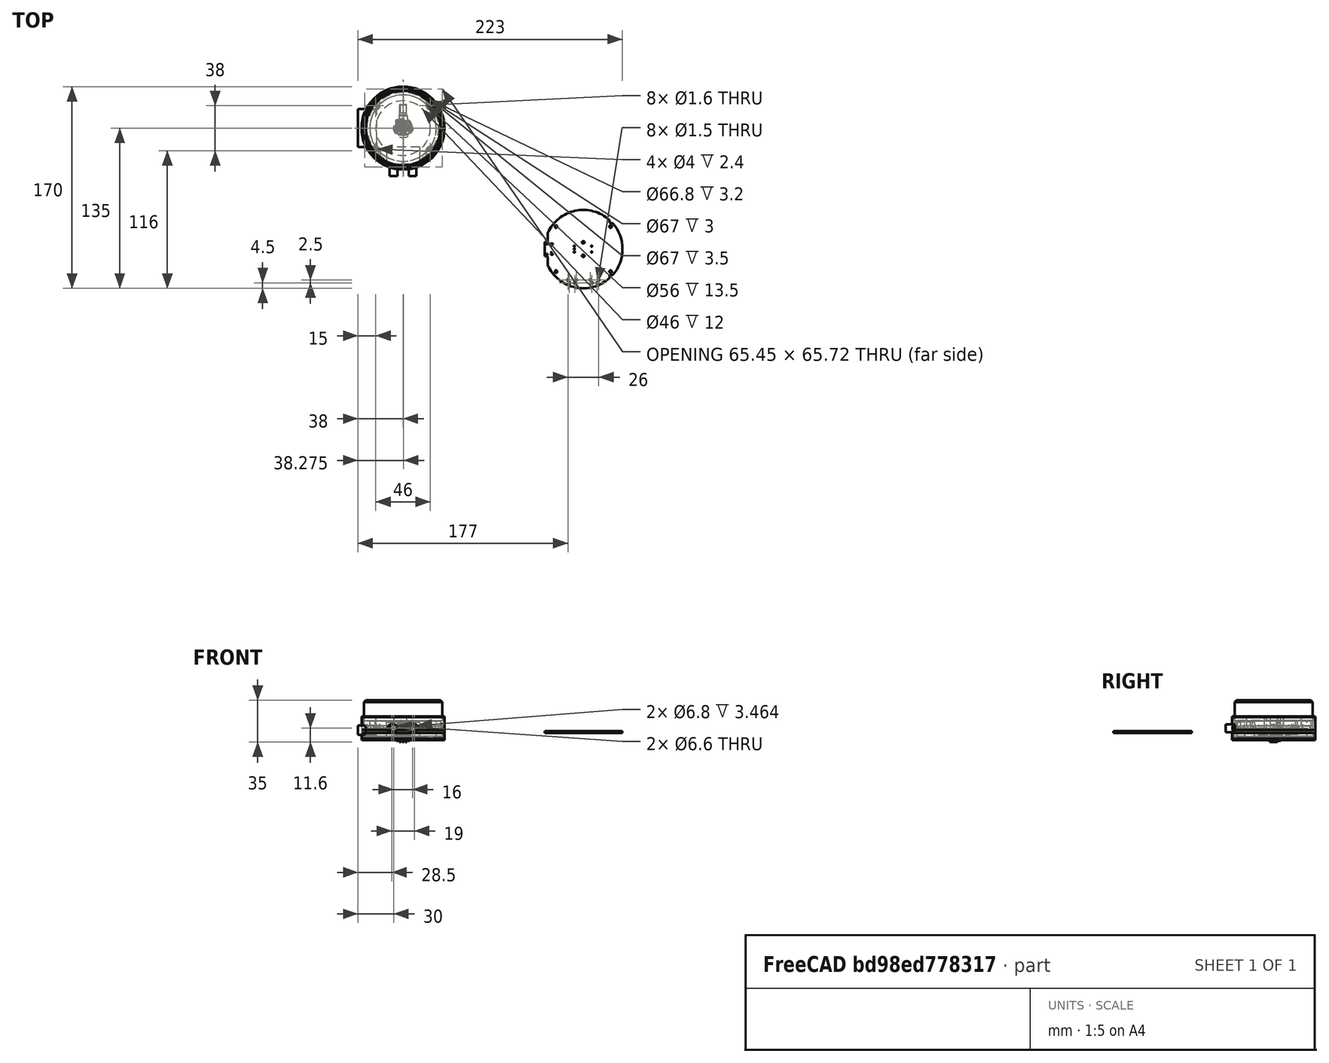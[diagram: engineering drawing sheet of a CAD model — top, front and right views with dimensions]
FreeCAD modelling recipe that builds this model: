
FCSTD DOCUMENT  (FreeCAD 0.18R4 (GitTag))
Label: USBVolumeKnob
License: All rights reserved
LicenseURL: http://en.wikipedia.org/wiki/All_rights_reserved
objects: App::Part×79, Part::Feature×75, Sketcher::SketchObject×22, PartDesign::Pad×10, PartDesign::Pocket×10, PartDesign::Body×6, Mesh::Feature×3, PartDesign::Boolean×2, PartDesign::Revolution×1, PartDesign::Chamfer×1
note: 148 computed .brp shape members not serialized (recipe doc carries the construction recipe); baked Part::Feature solids carry a one-line shape summary decoded from their .brp

FEATURE [Sketcher::SketchObject] Sketch
  MapMode = 5
  Support = -> [XY_Plane028]
  sketch-geometry (1):
    g0: Circle CenterX=0 CenterY=0 CenterZ=0 NormalX=0 NormalY=0 NormalZ=1 AngleXU=0 Radius=33
  constraints (1):
    c: Diameter(g0) = 66
FEATURE [Sketcher::SketchObject] Sketch001
  MapMode = 5
  Support = -> [XY_Plane028]
  sketch-geometry (2):
    g0: ArcOfCircle CenterX=0 CenterY=0 CenterZ=0 NormalX=0 NormalY=0 NormalZ=1 AngleXU=0 Radius=3 StartAngle=4.18879 EndAngle=8.37758
    g1: LineSegment StartX=-1.5 StartY=2.59808 StartZ=0 EndX=-1.5 EndY=-2.59808 EndZ=0
  constraints (7):
    c: Vertical(g1)
    c: Coincident(g0,g1)
    c: Coincident(g0,g1)
    c: Radius(g0) = 3
    c: Coincident(g1,g0)
    c: Coincident(g0,g-1)
    c: DistanceX(g0,g0) = 1.5
FEATURE [PartDesign::Pad] Pad
  Length = 26
  Length2 = 100
  Profile = -> Sketch
  Type = 0
FEATURE [Sketcher::SketchObject] Sketch002
  MapMode = 5
  Placement = pos=(0,0,0) rot=(1,0,0;3.14159rad)
  Support = -> [Pad]
  sketch-geometry (2):
    g0: Circle CenterX=0 CenterY=0 CenterZ=0 NormalX=0 NormalY=0 NormalZ=1 AngleXU=0 Radius=23
    g1: Circle CenterX=0 CenterY=0 CenterZ=0 NormalX=0 NormalY=0 NormalZ=1 AngleXU=0 Radius=8
  constraints (4):
    c: Diameter(g0) = 46
    c: Coincident(g0,g-1)
    c: Diameter(g1) = 16
    c: Coincident(g1,g0)
FEATURE [PartDesign::Pocket] Pocket
  BaseFeature = -> Pad
  Length = 12
  Length2 = 100
  Profile = -> Sketch001
  Reversed = true
  Type = 0
FEATURE [PartDesign::Pocket] Pocket001
  BaseFeature = -> Pocket
  Length = 12
  Length2 = 100
  Profile = -> Sketch002
  Type = 0
FEATURE [Sketcher::SketchObject] Sketch003
  MapMode = 5
  Placement = pos=(0,0,0) rot=(1,0,0;3.14159rad)
  Support = -> [Pocket001]
  sketch-geometry (1):
    g0: Circle CenterX=0 CenterY=0 CenterZ=0 NormalX=0 NormalY=0 NormalZ=1 AngleXU=0 Radius=8
  constraints (2):
    c: Diameter(g0) = 16
    c: Coincident(g0,g-1)
FEATURE [PartDesign::Pocket] Pocket002
  BaseFeature = -> Pocket001
  Length = 2
  Length2 = 100
  Profile = -> Sketch003
  Type = 0
FEATURE [Sketcher::SketchObject] Sketch004
  MapMode = 5
  Support = -> [XY_Plane053]
  sketch-geometry (2):
    g0: ArcOfCircle CenterX=0 CenterY=0 CenterZ=0 NormalX=0 NormalY=0 NormalZ=1 AngleXU=0 Radius=33 StartAngle=3.32443 EndAngle=9.24194
    g1: LineSegment StartX=-32.45 StartY=6 StartZ=0 EndX=-32.45 EndY=-6 EndZ=0
  constraints (7):
    c: Diameter(g0) = 66
    c: Coincident(g0,g-1)
    c: Vertical(g1)
    c: Coincident(g0,g1)
    c: Coincident(g0,g1)
    c: DistanceY(g1,g1) = 12
    c: Coincident(g0,g1)
FEATURE [PartDesign::Pad] Pad001
  Length = 4
  Length2 = 100
  Profile = -> Sketch004
  Type = 0
FEATURE [Sketcher::SketchObject] Sketch006
  MapMode = 5
  Placement = pos=(0,0,0) rot=(1,0,0;1.5708rad)
  Support = -> [XZ_Plane055]
  sketch-geometry (8):
    g0: LineSegment StartX=-35 StartY=-6 StartZ=0 EndX=-33.5 EndY=-6 EndZ=0
    g1: LineSegment StartX=-33.5 StartY=-6 StartZ=0 EndX=-33.5 EndY=-3 EndZ=0
    g2: LineSegment StartX=-33.5 StartY=-3 StartZ=0 EndX=-28 EndY=-3 EndZ=0
    g3: LineSegment StartX=-28 StartY=-3 StartZ=0 EndX=-28 EndY=10.5 EndZ=0
    g4: LineSegment StartX=-28 StartY=10.5 StartZ=0 EndX=-33.5 EndY=10.5 EndZ=0
    g5: LineSegment StartX=-33.5 StartY=10.5 StartZ=0 EndX=-33.5 EndY=14 EndZ=0
    g6: LineSegment StartX=-33.5 StartY=14 StartZ=0 EndX=-35 EndY=14 EndZ=0
    g7: LineSegment StartX=-35 StartY=14 StartZ=0 EndX=-35 EndY=-6 EndZ=0
  constraints (24):
    c: Coincident(g0,g1)
    c: Coincident(g2,g3)
    c: Coincident(g3,g4)
    c: Coincident(g4,g5)
    c: Coincident(g5,g6)
    c: Coincident(g6,g7)
    c: Coincident(g7,g0)
    c: Vertical(g3)
    c: Vertical(g7)
    c: Horizontal(g6)
    c: Horizontal(g4)
    c: Horizontal(g2)
    c: Horizontal(g0)
    c: Vertical(g1)
    c: Vertical(g5)
    c: DistanceX(g0,g-1) = 35
    c: DistanceX(g0,g-1) = 33.5
    c: DistanceX(g2,g-1) = 28
    c: DistanceX(g5,g-1) = 33.5
    c: DistanceY(g0,g-1) = 6
    c: DistanceY(g1,g-1) = 3
    c: DistanceY(g-1,g3) = 10.5
    c: DistanceY(g-1,g6) = 14
    c: Coincident(g2,g1)
FEATURE [PartDesign::Revolution] Revolution
  Angle = 360
  Axis = (0,-2e-16,1)
  Base = (0,0,0)
  Placement = pos=(0,0,0) rot=(1,0,0;1.5708rad)
  Profile = -> Sketch006
  ReferenceAxis = -> Sketch006 [V_Axis]
FEATURE [Sketcher::SketchObject] Sketch007
  MapMode = 5
  Placement = pos=(0,0,0) rot=(1,0,0;1.5708rad)
  Support = -> [XZ_Plane056]
  sketch-geometry (4):
    g0: LineSegment StartX=-14 StartY=-4 StartZ=0 EndX=-14 EndY=9 EndZ=0
    g1: LineSegment StartX=-14 StartY=9 StartZ=0 EndX=14 EndY=9 EndZ=0
    g2: LineSegment StartX=14 StartY=9 StartZ=0 EndX=14 EndY=-4 EndZ=0
    g3: LineSegment StartX=14 StartY=-4 StartZ=0 EndX=-14 EndY=-4 EndZ=0
  constraints (12):
    c: Coincident(g0,g1)
    c: Coincident(g1,g2)
    c: Coincident(g2,g3)
    c: Coincident(g3,g0)
    c: Vertical(g0)
    c: Vertical(g2)
    c: Horizontal(g1)
    c: Horizontal(g3)
    c: DistanceY(g2,g1) = 13
    c: DistanceX(g-1,g1) = 14
    c: DistanceX(g0,g-1) = 14
    c: DistanceY(g2,g-1) = 4
FEATURE [PartDesign::Pad] Pad003
  Length = 14.5
  Length2 = 100
  Placement = pos=(0,0,0) rot=(1,0,0;1.5708rad)
  Profile = -> Sketch007
  Type = 0
FEATURE [Sketcher::SketchObject] Sketch008
  MapMode = 5
  Placement = pos=(0,-14.5,6.4e-15) rot=(1,0,0;1.5708rad)
  Support = -> [Pad003]
  sketch-geometry (2):
    g0: Circle CenterX=-8 CenterY=4 CenterZ=0 NormalX=0 NormalY=0 NormalZ=1 AngleXU=0 Radius=3.3
    g1: Circle CenterX=8 CenterY=4 CenterZ=0 NormalX=0 NormalY=0 NormalZ=1 AngleXU=0 Radius=3.3
  constraints (6):
    c: Radius(g0) = 3.3
    c: Radius(g1) = 3.3
    c: DistanceX(g-1,g1) = 8
    c: DistanceX(g0,g-1) = 8
    c: DistanceY(g-1,g0) = 4
    c: DistanceY(g-1,g1) = 4
FEATURE [PartDesign::Pad] Pad004
  BaseFeature = -> Pad003
  Length = 10
  Length2 = 100
  Placement = pos=(0,0,0) rot=(1,0,0;1.5708rad)
  Profile = -> Sketch008
  Type = 0
FEATURE [PartDesign::Body] Body003
  Group = -> [Sketch007,Pad003,Sketch008,Pad004]
  Origin = -> Origin056
  Placement = pos=(0,-16,0) rot=(0,0,1;0rad)
  Tip = -> Pad004
FEATURE [PartDesign::Boolean] Boolean
  BaseFeature = -> Revolution
  Group = -> [Body003]
  Type = 1
FEATURE [Sketcher::SketchObject] Sketch009
  MapMode = 5
  Placement = pos=(0,0,0) rot=(0.57735,0.57735,0.57735;2.0944rad)
  Support = -> [YZ_Plane057]
  sketch-geometry (4):
    g0: ArcOfCircle CenterX=-12 CenterY=2.4 CenterZ=0 NormalX=0 NormalY=0 NormalZ=1 AngleXU=0 Radius=4 StartAngle=1.5708 EndAngle=4.71239
    g1: ArcOfCircle CenterX=12 CenterY=2.4 CenterZ=0 NormalX=0 NormalY=0 NormalZ=1 AngleXU=0 Radius=4 StartAngle=4.71239 EndAngle=7.85398
    g2: LineSegment StartX=-12 StartY=-1.6 StartZ=0 EndX=12 EndY=-1.6 EndZ=0
    g3: LineSegment StartX=-12 StartY=6.4 StartZ=0 EndX=12 EndY=6.4 EndZ=0
  constraints (10):
    c: Tangent(g0,g3) = 1.5708
    c: Tangent(g0,g2) = -1.5708
    c: Tangent(g2,g1) = -1.5708
    c: Tangent(g3,g1) = 1.5708
    c: Horizontal(g2)
    c: Equal(g0,g1)
    c: Radius(g1) = 4
    c: DistanceX(g0,g1) = 24
    c: DistanceX(g-1,g1) = 12
    c: DistanceY(g1,g-1) = 1.6
FEATURE [PartDesign::Pad] Pad005
  Length = 16
  Length2 = 100
  Placement = pos=(0,0,0) rot=(0.57735,0.57735,0.57735;2.0944rad)
  Profile = -> Sketch009
  Reversed = true
  Type = 0
FEATURE [PartDesign::Body] Body004
  Group = -> [Sketch009,Pad005]
  Origin = -> Origin057
  Placement = pos=(-22,0,0) rot=(0,0,1;0rad)
  Tip = -> Pad005
FEATURE [PartDesign::Boolean] Boolean001
  BaseFeature = -> Boolean
  Group = -> [Body004]
  Type = 1
FEATURE [PartDesign::Body] Body002
  Group = -> [Sketch006,Revolution,Boolean,Boolean001]
  Origin = -> Origin055
  Tip = -> Boolean001
FEATURE [App::Part] Part003  label="OldMidFrame"
  Group = -> [Body002]
  Origin = -> Origin054
FEATURE [Part::Feature] Part__Feature017  label="SOLID014"
  shape: bbox 1.6 x 0.8 x 0.45 mm, 26 faces (baked)
FEATURE [Part::Feature] Part__Feature029  label="SOLID026"
  shape: bbox 1.6 x 0.8 x 0.45 mm, 26 faces (baked)
FEATURE [Part::Feature] Part__Feature037  label="SOLID034"
  shape: bbox 1.6 x 0.8 x 0.8 mm, 28 faces (baked)
FEATURE [Part::Feature] Part__Feature005  label="SOLID003"
  shape: bbox 10.15 x 5.2 x 3.4 mm, 195 faces (baked)
FEATURE [Part::Feature] Part__Feature054  label="SOLID051"
  shape: bbox 1.6 x 0.8 x 0.8 mm, 28 faces (baked)
FEATURE [Part::Feature] Part__Feature032  label="SOLID029"
  shape: bbox 1.6 x 0.8 x 0.45 mm, 26 faces (baked)
FEATURE [Part::Feature] Part__Feature058  label="SOLID055"
  shape: bbox 1.6 x 0.8 x 0.8 mm, 28 faces (baked)
FEATURE [Part::Feature] Part__Feature057  label="SOLID054"
  shape: bbox 2 x 1.25 x 1.25 mm, 28 faces (baked)
FEATURE [Part::Feature] Part__Feature025  label="SOLID022"
  shape: bbox 1.6 x 0.8 x 0.45 mm, 26 faces (baked)
FEATURE [Part::Feature] Part__Feature004  label="SOLID002"
  shape: bbox 16.4 x 5.2 x 3.4 mm, 320 faces (baked)
FEATURE [Part::Feature] Part__Feature049  label="SOLID046"
  shape: bbox 1 x 0.5 x 0.5 mm, 28 faces (baked)
FEATURE [Part::Feature] Part__Feature011  label="SOLID009"
  shape: bbox 7 x 6.5 x 1.7 mm, 78 faces (baked)
FEATURE [Part::Feature] Part__Feature013  label="SOLID011"
  shape: bbox 4 x 2.5 x 1.59 mm, 242 faces (baked)
FEATURE [Part::Feature] Part__Feature014  label="COMPOUND002"
  shape: bbox 8.7 x 10.9 x 12.85 mm, 158 faces, 3 solids (baked)
FEATURE [Part::Feature] Part__Feature002  label="SOLID"
  shape: bbox 14 x 23.5 x 14.75 mm, 198 faces (baked)
FEATURE [Part::Feature] Part__Feature016  label="SOLID013"
  shape: bbox 1.6 x 0.8 x 0.45 mm, 26 faces (baked)
FEATURE [Part::Feature] Part__Feature008  label="SOLID006"
  shape: bbox 12 x 12 x 1.5 mm, 1004 faces (baked)
FEATURE [Part::Feature] Part__Feature001  label="COMPOUND001"
  shape: bbox 6.35 x 6.121 x 5.842 mm, 252 faces, 3 solids (baked)
FEATURE [Part::Feature] Part__Feature006  label="SOLID004"
  shape: bbox 5 x 1.113 x 3.175 mm, 141 faces (baked)
FEATURE [Part::Feature] Part__Feature010  label="SOLID008"
  shape: bbox 2.8 x 2.9 x 1.55 mm, 109 faces (baked)
FEATURE [App::Part] Molex_PicoBlade_53261_0471_1x04_1MP_P1_25mm_Horizontal  label="Molex_PicoBlade_53261-0471_1x04-1MP_P1.25mm_Horizontal"
  Group = -> [Part__Feature005]
  Origin = -> Origin006
  Placement = pos=(176.75,-93,1.65) rot=(0,0,1;1.5708rad)
FEATURE [App::Part] SOT_23_5001  label="SOT-23-007"
  Group = -> [Part__Feature010]
  Origin = -> Origin011
  Placement = pos=(169,-80.25,1.65) rot=(0,0,1;0rad)
FEATURE [App::Part] SW_SPST_B3U_1000P001  label="SW_SPST_B3U-1000P001"
  Group = -> [Part__Feature013]
  Origin = -> Origin014
  Placement = pos=(164,-96,1.65) rot=(0,0,-1;1.5708rad)
FEATURE [App::Part] SOT_223  label="SOT-223"
  Group = -> [Part__Feature011]
  Origin = -> Origin012
  Placement = pos=(136.5,-110,1.65) rot=(0,0,1;0rad)
FEATURE [App::Part] FTSH_105_01_L_DV_K  label="FTSH-105-01-L-DV-K"
  Group = -> [Part__Feature001]
  Origin = -> Origin002
  Placement = pos=(135.75,-83,2.05) rot=(-0.57735,0.57735,0.57735;4.18879rad)
FEATURE [App::Part] pec12r_4020f_n0024  label="pec12r-4020f-n0024"
  Group = -> [Part__Feature002]
  Origin = -> Origin003
  Placement = pos=(152,-102,1.65) rot=(0.57735,0.57735,0.57735;2.0944rad)
FEATURE [App::Part] Molex_PicoBlade_53261_0971_1x09_1MP_P1_25mm_Horizontal  label="Molex_PicoBlade_53261-0971_1x09-1MP_P1.25mm_Horizontal"
  Group = -> [Part__Feature004]
  Origin = -> Origin005
  Placement = pos=(176.75,-108.25,1.65) rot=(0,0,1;1.5708rad)
FEATURE [App::Part] ABM3B_18_432MHZ_B2  label="ABM3B-18.432MHZ-B2"
  Group = -> [Part__Feature006]
  Origin = -> Origin007
  Placement = pos=(163.25,-87,1.65) rot=(-0.57735,0.57735,0.57735;4.18879rad)
FEATURE [App::Part] LQFP_64_10x10mm_P0_5mm  label="LQFP-64_10x10mm_P0.5mm"
  Group = -> [Part__Feature008]
  Origin = -> Origin009
  Placement = pos=(149.5,-84.5,1.65) rot=(0,0,1;3.14159rad)
FEATURE [App::Part] B3F_3152__3DModel_STEP_273799  label="B3F-3152--3DModel-STEP-273799"
  Group = -> [Part__Feature014]
  Origin = -> Origin015
  Placement = pos=(163.75,-130.5,1.65) rot=(1,0,0;1.5708rad)
FEATURE [App::Part] R_0603_1608Metric001
  Group = -> [Part__Feature016]
  Origin = -> Origin017
  Placement = pos=(171.5,-111.75,1.65) rot=(0,0,1;1.5708rad)
FEATURE [App::Part] R_0603_1608Metric002
  Group = -> [Part__Feature017]
  Origin = -> Origin018
  Placement = pos=(130.5,-104.75,1.65) rot=(0,0,1;0rad)
FEATURE [App::Part] R_0603_1608Metric010
  Group = -> [Part__Feature025]
  Origin = -> Origin026
  Placement = pos=(162,-91.75,1.65) rot=(0,0,1;1.5708rad)
FEATURE [App::Part] R_0603_1608Metric017
  Group = -> [Part__Feature032]
  Origin = -> Origin033
  Placement = pos=(161.5,-122.75,1.65) rot=(0,0,1;1.5708rad)
FEATURE [App::Part] C_0603_1608Metric
  Group = -> [Part__Feature037]
  Origin = -> Origin038
  Placement = pos=(168.5,-92.5,-0.05) rot=(0.866025,-0.5,0;3.14159rad)
FEATURE [App::Part] R_0603_1608Metric014
  Group = -> [Part__Feature029]
  Origin = -> Origin030
  Placement = pos=(139,-93,1.65) rot=(0,0,1;3.14159rad)
FEATURE [App::Part] C_0603_1608Metric016
  Group = -> [Part__Feature058]
  Origin = -> Origin059
  Placement = pos=(169,-91,1.65) rot=(0,0,1;1.5708rad)
FEATURE [App::Part] C_0603_1608Metric015
  Group = -> [Part__Feature054]
  Origin = -> Origin079
  Placement = pos=(166.5,-84.5,1.65) rot=(0,0,1;1.5708rad)
FEATURE [App::Part] C_0805_2012Metric002
  Group = -> [Part__Feature057]
  Origin = -> Origin058
  Placement = pos=(130.75,-112,1.65) rot=(0,0,1;1.5708rad)
FEATURE [App::Part] C_0402_1005Metric001
  Group = -> [Part__Feature049]
  Origin = -> Origin050
  Placement = pos=(160.25,-88.25,1.65) rot=(0,0,1;1.5708rad)
FEATURE [Part::Feature] Part__Feature  label="COMPOUND"
  shape: bbox 8.941 x 4.361 x 6.901 mm, 1244 faces, 44 solids (baked)
FEATURE [App::Part] DX07S016JA1R1500__3DModel_STEP_1  label="DX07S016JA1R1500--3DModel-STEP-1"
  Group = -> [Part__Feature]
  Origin = -> Origin001
  Placement = pos=(122.75,-102,1.75) rot=(-0.57735,0.57735,0.57735;4.18879rad)
FEATURE [Part::Feature] Part__Feature003  label="SOLID001"
  shape: bbox 5.4 x 5 x 1.5 mm, 60 faces (baked)
FEATURE [App::Part] LED_RGB_5050_6  label="LED_RGB_5050-6"
  Group = -> [Part__Feature003]
  Origin = -> Origin004
  Placement = pos=(132,-113.5,-0.05) rot=(0.866025,-0.5,0;3.14159rad)
FEATURE [Part::Feature] Part__Feature012  label="SOLID010"
  shape: bbox 4 x 2.5 x 1.59 mm, 242 faces (baked)
FEATURE [App::Part] SW_SPST_B3U_1000P  label="SW_SPST_B3U-1000P"
  Group = -> [Part__Feature012]
  Origin = -> Origin013
  Placement = pos=(168.75,-96,1.65) rot=(0,0,-1;1.5708rad)
FEATURE [Part::Feature] Part__Feature074  label="COMPOUND004"
  shape: bbox 65.6 x 66 x 1.6 mm, 61 faces (baked)
FEATURE [Part::Feature] Part__Feature070  label="SOLID066"
  shape: bbox 5.4 x 5 x 1.5 mm, 60 faces (baked)
FEATURE [App::Part] LED_RGB_5050_6005  label="LED_RGB_5050-011"
  Group = -> [Part__Feature070]
  Origin = -> Origin071
  Placement = pos=(152,-125,-0.05) rot=(1,0,0;3.14159rad)
FEATURE [Part::Feature] Part__Feature069  label="SOLID065"
  shape: bbox 1.6 x 0.8 x 0.45 mm, 26 faces (baked)
FEATURE [App::Part] R_0603_1608Metric024
  Group = -> [Part__Feature069]
  Origin = -> Origin070
  Placement = pos=(142.5,-122.75,1.65) rot=(0,0,1;1.5708rad)
FEATURE [Part::Feature] Part__Feature071  label="SOLID067"
  shape: bbox 1.6 x 0.8 x 0.8 mm, 28 faces (baked)
FEATURE [App::Part] C_0603_1608Metric019
  Group = -> [Part__Feature071]
  Origin = -> Origin072
  Placement = pos=(163,-122.75,1.65) rot=(0,0,-1;1.5708rad)
FEATURE [Part::Feature] Part__Feature060  label="SOLID057"
  shape: bbox 1.6 x 0.8 x 0.8 mm, 28 faces (baked)
FEATURE [App::Part] C_0603_1608Metric017
  Group = -> [Part__Feature060]
  Origin = -> Origin061
  Placement = pos=(139,-94.5,1.65) rot=(0,0,1;3.14159rad)
FEATURE [Part::Feature] Part__Feature064  label="SOLID060"
  shape: bbox 1.6 x 0.8 x 0.45 mm, 26 faces (baked)
FEATURE [App::Part] R_0603_1608Metric019
  Group = -> [Part__Feature064]
  Origin = -> Origin065
  Placement = pos=(139,-100.5,1.65) rot=(0,0,1;3.14159rad)
FEATURE [Part::Feature] Part__Feature053  label="SOLID050"
  shape: bbox 1.6 x 0.8 x 0.8 mm, 28 faces (baked)
FEATURE [App::Part] C_0603_1608Metric014
  Group = -> [Part__Feature053]
  Origin = -> Origin076
  Placement = pos=(158.75,-81.5,1.65) rot=(0,0,1;0rad)
FEATURE [Part::Feature] Part__Feature059  label="SOLID056"
  shape: bbox 2 x 1.25 x 1.25 mm, 28 faces (baked)
FEATURE [App::Part] C_0805_2012Metric003
  Group = -> [Part__Feature059]
  Origin = -> Origin060
  Placement = pos=(130.75,-108,1.65) rot=(0,0,-1;1.5708rad)
FEATURE [Part::Feature] Part__Feature065  label="SOLID061"
  shape: bbox 1.6 x 0.8 x 0.45 mm, 26 faces (baked)
FEATURE [App::Part] R_0603_1608Metric020
  Group = -> [Part__Feature065]
  Origin = -> Origin066
  Placement = pos=(139,-99,1.65) rot=(0,0,1;3.14159rad)
FEATURE [Part::Feature] Part__Feature067  label="SOLID063"
  shape: bbox 1.6 x 0.8 x 0.45 mm, 26 faces (baked)
FEATURE [App::Part] R_0603_1608Metric022
  Group = -> [Part__Feature067]
  Origin = -> Origin068
  Placement = pos=(139,-97.5,1.65) rot=(0,0,1;0rad)
FEATURE [Part::Feature] Part__Feature061  label="SOLID058"
  shape: bbox 1.6 x 0.8 x 0.8 mm, 28 faces (baked)
FEATURE [App::Part] C_0603_1608Metric018
  Group = -> [Part__Feature061]
  Origin = -> Origin062
  Placement = pos=(139,-96,1.65) rot=(0,0,1;3.14159rad)
FEATURE [Part::Feature] Part__Feature063  label="COMPOUND003"
  shape: bbox 8.7 x 10.9 x 12.85 mm, 158 faces, 3 solids (baked)
FEATURE [App::Part] B3F_3152__3DModel_STEP_273799001  label="B3F-3152--3DModel-STEP-273800"
  Group = -> [Part__Feature063]
  Origin = -> Origin064
  Placement = pos=(144.75,-130.5,1.65) rot=(1,0,0;1.5708rad)
FEATURE [Part::Feature] Part__Feature068  label="SOLID064"
  shape: bbox 1.6 x 0.8 x 0.45 mm, 26 faces (baked)
FEATURE [App::Part] R_0603_1608Metric023
  Group = -> [Part__Feature068]
  Origin = -> Origin069
  Placement = pos=(141,-122.75,1.65) rot=(0,0,-1;1.5708rad)
FEATURE [Part::Feature] Part__Feature066  label="SOLID062"
  shape: bbox 1.6 x 0.8 x 0.45 mm, 26 faces (baked)
FEATURE [App::Part] R_0603_1608Metric021
  Group = -> [Part__Feature066]
  Origin = -> Origin067
  Placement = pos=(139,-102,1.65) rot=(0,0,1;0rad)
FEATURE [Part::Feature] Part__Feature055  label="SOLID052"
  shape: bbox 2 x 1.25 x 1.25 mm, 28 faces (baked)
FEATURE [App::Part] C_0805_2012Metric
  Group = -> [Part__Feature055]
  Origin = -> Origin080
  Placement = pos=(148.5,-75,1.65) rot=(0,0,1;1.5708rad)
FEATURE [Part::Feature] Part__Feature052  label="SOLID049"
  shape: bbox 1.6 x 0.8 x 0.8 mm, 28 faces (baked)
FEATURE [App::Part] C_0603_1608Metric013
  Group = -> [Part__Feature052]
  Origin = -> Origin077
  Placement = pos=(158.75,-80,1.65) rot=(0,0,1;0rad)
FEATURE [Part::Feature] Part__Feature062  label="SOLID059"
  shape: bbox 1.6 x 0.8 x 0.45 mm, 26 faces (baked)
FEATURE [App::Part] R_0603_1608Metric018
  Group = -> [Part__Feature062]
  Origin = -> Origin063
  Placement = pos=(130.5,-99.25,1.65) rot=(0,0,1;0rad)
FEATURE [Part::Feature] Part__Feature042  label="SOLID039"
  shape: bbox 1.6 x 0.8 x 0.8 mm, 28 faces (baked)
FEATURE [App::Part] C_0603_1608Metric005
  Group = -> [Part__Feature042]
  Origin = -> Origin043
  Placement = pos=(152,-83,-0.05) rot=(1,0,0;3.14159rad)
FEATURE [Part::Feature] Part__Feature046  label="SOLID043"
  shape: bbox 1.6 x 0.8 x 0.8 mm, 28 faces (baked)
FEATURE [App::Part] C_0603_1608Metric009
  Group = -> [Part__Feature046]
  Origin = -> Origin047
  Placement = pos=(144,-75.25,1.65) rot=(0,0,1;1.5708rad)
FEATURE [Part::Feature] Part__Feature051  label="SOLID048"
  shape: bbox 1.6 x 0.8 x 0.8 mm, 28 faces (baked)
FEATURE [App::Part] C_0603_1608Metric012
  Group = -> [Part__Feature051]
  Origin = -> Origin052
  Placement = pos=(157.75,-90.5,1.65) rot=(0,0,-1;1.5708rad)
FEATURE [Part::Feature] Part__Feature040  label="SOLID037"
  shape: bbox 1.6 x 0.8 x 0.8 mm, 28 faces (baked)
FEATURE [App::Part] C_0603_1608Metric003
  Group = -> [Part__Feature040]
  Origin = -> Origin041
  Placement = pos=(135.5,-111.5,-0.05) rot=(0.5,0.866025,0;3.14159rad)
FEATURE [Part::Feature] Part__Feature041  label="SOLID038"
  shape: bbox 1.6 x 0.8 x 0.8 mm, 28 faces (baked)
FEATURE [App::Part] C_0603_1608Metric004
  Group = -> [Part__Feature041]
  Origin = -> Origin042
  Placement = pos=(135.5,-92.5,-0.05) rot=(0.866025,0.5,0;3.14159rad)
FEATURE [Part::Feature] Part__Feature036  label="SOLID033"
  shape: bbox 5.4 x 5 x 1.5 mm, 60 faces (baked)
FEATURE [App::Part] LED_RGB_5050_6004  label="LED_RGB_5050-010"
  Group = -> [Part__Feature036]
  Origin = -> Origin037
  Placement = pos=(152,-79,-0.05) rot=(0,1,0;3.14159rad)
FEATURE [Part::Feature] Part__Feature043  label="SOLID040"
  shape: bbox 1.6 x 0.8 x 0.8 mm, 28 faces (baked)
FEATURE [App::Part] C_0603_1608Metric006
  Group = -> [Part__Feature043]
  Origin = -> Origin044
  Placement = pos=(168.25,-77.5,1.65) rot=(0,0,1;3.14159rad)
FEATURE [Part::Feature] Part__Feature047  label="SOLID044"
  shape: bbox 1.6 x 0.8 x 0.8 mm, 28 faces (baked)
FEATURE [App::Part] C_0603_1608Metric010
  Group = -> [Part__Feature047]
  Origin = -> Origin048
  Placement = pos=(141.25,-89,1.65) rot=(0,0,1;1.5708rad)
FEATURE [Part::Feature] Part__Feature038  label="SOLID035"
  shape: bbox 1.6 x 0.8 x 0.8 mm, 28 faces (baked)
FEATURE [App::Part] C_0603_1608Metric001
  Group = -> [Part__Feature038]
  Origin = -> Origin039
  Placement = pos=(168.5,-111.5,-0.05) rot=(-0.5,0.866025,0;3.14159rad)
FEATURE [Part::Feature] Part__Feature039  label="SOLID036"
  shape: bbox 1.6 x 0.8 x 0.8 mm, 28 faces (baked)
FEATURE [App::Part] C_0603_1608Metric002
  Group = -> [Part__Feature039]
  Origin = -> Origin040
  Placement = pos=(152,-121,-0.05) rot=(0,1,0;3.14159rad)
FEATURE [Part::Feature] Part__Feature045  label="SOLID042"
  shape: bbox 1.6 x 0.8 x 0.8 mm, 28 faces (baked)
FEATURE [App::Part] C_0603_1608Metric008
  Group = -> [Part__Feature045]
  Origin = -> Origin046
  Placement = pos=(153.5,-76.25,1.65) rot=(0,0,1;0rad)
FEATURE [Part::Feature] Part__Feature048  label="SOLID045"
  shape: bbox 1 x 0.5 x 0.5 mm, 28 faces (baked)
FEATURE [App::Part] C_0402_1005Metric
  Group = -> [Part__Feature048]
  Origin = -> Origin049
  Placement = pos=(160.25,-86,1.65) rot=(0,0,1;1.5708rad)
FEATURE [Part::Feature] Part__Feature050  label="SOLID047"
  shape: bbox 1.6 x 0.8 x 0.8 mm, 28 faces (baked)
FEATURE [App::Part] C_0603_1608Metric011
  Group = -> [Part__Feature050]
  Origin = -> Origin051
  Placement = pos=(155.25,-92.75,1.65) rot=(0,0,1;3.14159rad)
FEATURE [Part::Feature] Part__Feature073  label="SOLID069"
  shape: bbox 1.6 x 0.8 x 0.8 mm, 28 faces (baked)
FEATURE [App::Part] C_0603_1608Metric021
  Group = -> [Part__Feature073]
  Origin = -> Origin074
  Placement = pos=(144,-122.75,1.65) rot=(0,0,-1;1.5708rad)
FEATURE [Part::Feature] Part__Feature022  label="SOLID019"
  shape: bbox 1.6 x 0.8 x 0.45 mm, 26 faces (baked)
FEATURE [App::Part] R_0603_1608Metric007
  Group = -> [Part__Feature022]
  Origin = -> Origin023
  Placement = pos=(163.25,-83.25,1.65) rot=(0,0,1;0rad)
FEATURE [Part::Feature] Part__Feature072  label="SOLID068"
  shape: bbox 1.6 x 0.8 x 0.8 mm, 28 faces (baked)
FEATURE [App::Part] C_0603_1608Metric020
  Group = -> [Part__Feature072]
  Origin = -> Origin073
  Placement = pos=(139,-103.5,1.65) rot=(0,0,1;3.14159rad)
FEATURE [Part::Feature] Part__Feature033  label="SOLID030"
  shape: bbox 5.4 x 5 x 1.5 mm, 60 faces (baked)
FEATURE [App::Part] LED_RGB_5050_6001  label="LED_RGB_5050-007"
  Group = -> [Part__Feature033]
  Origin = -> Origin034
  Placement = pos=(172,-90.5,-0.05) rot=(0.5,0.866025,0;3.14159rad)
FEATURE [Part::Feature] Part__Feature019  label="SOLID016"
  shape: bbox 1.6 x 0.8 x 0.45 mm, 26 faces (baked)
FEATURE [App::Part] R_0603_1608Metric004
  Group = -> [Part__Feature019]
  Origin = -> Origin020
  Placement = pos=(130.5,-95.75,1.65) rot=(0,0,1;3.14159rad)
FEATURE [Part::Feature] Part__Feature023  label="SOLID020"
  shape: bbox 1.6 x 0.8 x 0.45 mm, 26 faces (baked)
FEATURE [App::Part] R_0603_1608Metric008
  Group = -> [Part__Feature023]
  Origin = -> Origin024
  Placement = pos=(168.25,-84.5,1.65) rot=(0,0,1;1.5708rad)
FEATURE [Part::Feature] Part__Feature024  label="SOLID021"
  shape: bbox 1.6 x 0.8 x 0.45 mm, 26 faces (baked)
FEATURE [App::Part] R_0603_1608Metric009
  Group = -> [Part__Feature024]
  Origin = -> Origin083
  Placement = pos=(166.5,-88,1.65) rot=(0,0,1;1.5708rad)
FEATURE [Part::Feature] Part__Feature018  label="SOLID015"
  shape: bbox 1.6 x 0.8 x 0.45 mm, 26 faces (baked)
FEATURE [App::Part] R_0603_1608Metric003
  Group = -> [Part__Feature018]
  Origin = -> Origin019
  Placement = pos=(130.5,-97.5,1.65) rot=(0,0,1;0rad)
FEATURE [Part::Feature] Part__Feature021  label="SOLID018"
  shape: bbox 1.6 x 0.8 x 0.45 mm, 26 faces (baked)
FEATURE [App::Part] R_0603_1608Metric006
  Group = -> [Part__Feature021]
  Origin = -> Origin022
  Placement = pos=(152.75,-74.5,1.65) rot=(0,0,1;3.14159rad)
FEATURE [Part::Feature] Part__Feature027  label="SOLID024"
  shape: bbox 1.6 x 0.8 x 0.45 mm, 26 faces (baked)
FEATURE [App::Part] R_0603_1608Metric012
  Group = -> [Part__Feature027]
  Origin = -> Origin081
  Placement = pos=(134.75,-114.5,1.65) rot=(0,0,1;3.14159rad)
FEATURE [Part::Feature] Part__Feature031  label="SOLID028"
  shape: bbox 1.6 x 0.8 x 0.45 mm, 26 faces (baked)
FEATURE [App::Part] R_0603_1608Metric016
  Group = -> [Part__Feature031]
  Origin = -> Origin032
  Placement = pos=(160,-122.75,1.65) rot=(0,0,-1;1.5708rad)
FEATURE [Part::Feature] Part__Feature020  label="SOLID017"
  shape: bbox 1.6 x 0.8 x 0.45 mm, 26 faces (baked)
FEATURE [App::Part] R_0603_1608Metric005
  Group = -> [Part__Feature020]
  Origin = -> Origin021
  Placement = pos=(152.75,-73,1.65) rot=(0,0,1;0rad)
FEATURE [Part::Feature] Part__Feature026  label="SOLID023"
  shape: bbox 1.6 x 0.8 x 0.45 mm, 26 faces (baked)
FEATURE [App::Part] R_0603_1608Metric011
  Group = -> [Part__Feature026]
  Origin = -> Origin082
  Placement = pos=(170.5,-91,1.65) rot=(0,0,-1;1.5708rad)
FEATURE [Part::Feature] Part__Feature028  label="SOLID025"
  shape: bbox 1.6 x 0.8 x 0.45 mm, 26 faces (baked)
FEATURE [App::Part] R_0603_1608Metric013
  Group = -> [Part__Feature028]
  Origin = -> Origin029
  Placement = pos=(134.75,-105.5,1.65) rot=(0,0,1;3.14159rad)
FEATURE [Part::Feature] Part__Feature034  label="SOLID031"
  shape: bbox 5.4 x 5 x 1.5 mm, 60 faces (baked)
FEATURE [App::Part] LED_RGB_5050_6002  label="LED_RGB_5050-008"
  Group = -> [Part__Feature034]
  Origin = -> Origin035
  Placement = pos=(172,-113.5,-0.05) rot=(0.866025,0.5,0;3.14159rad)
FEATURE [Part::Feature] Part__Feature035  label="SOLID032"
  shape: bbox 5.4 x 5 x 1.5 mm, 60 faces (baked)
FEATURE [App::Part] LED_RGB_5050_6003  label="LED_RGB_5050-009"
  Group = -> [Part__Feature035]
  Origin = -> Origin036
  Placement = pos=(132,-90.5,-0.05) rot=(-0.5,0.866025,0;3.14159rad)
FEATURE [Part::Feature] Part__Feature044  label="SOLID041"
  shape: bbox 1.6 x 0.8 x 0.8 mm, 28 faces (baked)
FEATURE [App::Part] C_0603_1608Metric007
  Group = -> [Part__Feature044]
  Origin = -> Origin045
  Placement = pos=(162.75,-77.5,1.65) rot=(0,0,1;3.14159rad)
FEATURE [Part::Feature] Part__Feature007  label="SOLID005"
  shape: bbox 2.8 x 2.9 x 1.55 mm, 124 faces (baked)
FEATURE [App::Part] SOT_23_6  label="SOT-23-6"
  Group = -> [Part__Feature007]
  Origin = -> Origin008
  Placement = pos=(130.75,-102,1.65) rot=(0,0,1;0rad)
FEATURE [Part::Feature] Part__Feature009  label="SOLID007"
  shape: bbox 2.8 x 2.9 x 1.55 mm, 109 faces (baked)
FEATURE [App::Part] SOT_23_5  label="SOT-23-5"
  Group = -> [Part__Feature009]
  Origin = -> Origin010
  Placement = pos=(163.5,-80.25,1.65) rot=(0,0,1;0rad)
FEATURE [Part::Feature] Part__Feature015  label="SOLID012"
  shape: bbox 1.6 x 0.8 x 0.45 mm, 26 faces (baked)
FEATURE [App::Part] R_0603_1608Metric
  Group = -> [Part__Feature015]
  Origin = -> Origin016
  Placement = pos=(170,-111.75,1.65) rot=(0,0,1;1.5708rad)
FEATURE [Part::Feature] Part__Feature030  label="SOLID027"
  shape: bbox 1.6 x 0.8 x 0.45 mm, 26 faces (baked)
FEATURE [App::Part] R_0603_1608Metric015
  Group = -> [Part__Feature030]
  Origin = -> Origin031
  Placement = pos=(139,-91.5,1.65) rot=(0,0,1;3.14159rad)
FEATURE [Part::Feature] Part__Feature056  label="SOLID053"
  shape: bbox 2 x 1.25 x 1.25 mm, 28 faces (baked)
FEATURE [App::Part] C_0805_2012Metric001
  Group = -> [Part__Feature056]
  Origin = -> Origin078
  Placement = pos=(146.5,-75,1.65) rot=(0,0,1;1.5708rad)
FEATURE [App::Part] Open_CASCADE_STEP_translator_6_9_1  label="PCBA"
  Group = -> [DX07S016JA1R1500__3DModel_STEP_1,FTSH_105_01_L_DV_K,pec12r_4020f_n0024,LED_RGB_5050_6,Molex_PicoBlade_53261_0971_1x09_1MP_P1_25mm_Horizontal,Molex_PicoBlade_53261_0471_1x04_1MP_P1_25mm_Horizontal,ABM3B_18_432MHZ_B2,SOT_23_6,LQFP_64_10x10mm_P0_5mm,SOT_23_5,SOT_23_5001,SOT_223,SW_SPST_B3U_1000P,SW_SPST_B3U_1000P001,B3F_3152__3DModel_STEP_273799,R_0603_1608Metric,R_0603_1608Metric001,+58 more]
  Origin = -> Origin075
  Placement = pos=(-152,102,-1.6) rot=(0,0,1;0rad)
FEATURE [Sketcher::SketchObject] Sketch011  label="BoardOutline"
  MapMode = 5
  sketch-geometry (16):
    g0: ArcOfCircle CenterX=0 CenterY=0 CenterZ=0 NormalX=0 NormalY=0 NormalZ=1 AngleXU=0 Radius=33 StartAngle=3.57129 EndAngle=5.44212
    g1: LineSegment StartX=-32.6 StartY=6 StartZ=0 EndX=-32.6 EndY=-6 EndZ=0
    g2: LineSegment StartX=22 StartY=-24.5967 StartZ=0 EndX=22 EndY=-23 EndZ=0
    g3: LineSegment StartX=23 StartY=-22 StartZ=0 EndX=24.5967 EndY=-22 EndZ=0
    g4: ArcOfCircle CenterX=23 CenterY=-23 CenterZ=0 NormalX=0 NormalY=0 NormalZ=1 AngleXU=0 Radius=1 StartAngle=1.5708 EndAngle=3.14159
    g5: LineSegment StartX=22 StartY=24.5967 StartZ=0 EndX=22 EndY=23 EndZ=0
    g6: LineSegment StartX=23 StartY=22 StartZ=0 EndX=24.5967 EndY=22 EndZ=0
    g7: ArcOfCircle CenterX=23 CenterY=23 CenterZ=0 NormalX=0 NormalY=0 NormalZ=1 AngleXU=0 Radius=1 StartAngle=3.14159 EndAngle=4.71239
    g8: LineSegment StartX=-32.6 StartY=6 StartZ=0 EndX=-31 EndY=6 EndZ=0
    g9: LineSegment StartX=-30 StartY=7 StartZ=0 EndX=-30 EndY=13.7477 EndZ=0
    g10: ArcOfCircle CenterX=-31 CenterY=7 CenterZ=0 NormalX=0 NormalY=0 NormalZ=1 AngleXU=0 Radius=1 StartAngle=4.71239 EndAngle=6.28319
    g11: LineSegment StartX=-32.6 StartY=-6 StartZ=0 EndX=-31 EndY=-6 EndZ=0
    g12: LineSegment StartX=-30 StartY=-7 StartZ=0 EndX=-30 EndY=-13.7477 EndZ=0
    g13: ArcOfCircle CenterX=-31 CenterY=-7 CenterZ=0 NormalX=0 NormalY=0 NormalZ=1 AngleXU=0 Radius=1 StartAngle=0 EndAngle=1.5708
    g14: ArcOfCircle CenterX=0 CenterY=0 CenterZ=0 NormalX=0 NormalY=0 NormalZ=1 AngleXU=0 Radius=33 StartAngle=5.55346 EndAngle=7.01291
    g15: ArcOfCircle CenterX=0 CenterY=0 CenterZ=0 NormalX=0 NormalY=0 NormalZ=1 AngleXU=0 Radius=33 StartAngle=0.841069 EndAngle=2.71189
  constraints (54):
    c: Radius(g0) = 33
    c: Coincident(g0,g-1)
    c: Radius(g4) = 1
    c: Coincident(g3,g4)
    c: Coincident(g2,g4)
    c: Vertical(g2)
    c: Horizontal(g3)
    c: Vertical(g1)
    c: DistanceX(g1,g0) = 32.6
    c: DistanceX(g2,g3) = 1
    c: DistanceY(g2,g3) = 1
    c: Coincident(g7,g5)
    c: Coincident(g7,g6)
    c: Radius(g7) = 1
    c: DistanceY(g6,g5) = 1
    c: DistanceX(g5,g6) = 1
    c: Horizontal(g6)
    c: Vertical(g5)
    c: PointOnObject(g6,g0)
    c: PointOnObject(g5,g0)
    c: DistanceY(g0,g6) = 22
    c: DistanceX(g0,g5) = 22
    c: Coincident(g10,g9)
    c: Coincident(g8,g10)
    c: Radius(g10) = 1
    c: DistanceX(g8,g9) = 1
    c: DistanceY(g8,g9) = 1
    c: Horizontal(g8)
    c: Vertical(g9)
    c: DistanceY(g0,g8) = 6
    c: Coincident(g1,g8)
    c: Coincident(g13,g12)
    c: Coincident(g11,g13)
    c: Radius(g13) = 1
    c: Horizontal(g11)
    c: Vertical(g12)
    c: Coincident(g1,g11)
    c: DistanceY(g12,g11) = 1
    c: DistanceX(g11,g12) = 1
    c: DistanceY(g1,g0) = 6
    c: Coincident(g15,g9)
    c: Coincident(g0,g12)
    c: Equal(g0,g14)
    c: Coincident(g0,g2)
    c: Coincident(g14,g3)
    c: Coincident(g0,g14)
    c: Equal(g14,g15)
    c: PointOnObject(g14,g6)
    c: PointOnObject(g15,g5)
    c: Coincident(g14,g15)
    c: DistanceX(g9,g0) = 30
    c: DistanceX(g0,g0) = 30
    c: DistanceX(g0,g0) = 22
    c: DistanceY(g3,g0) = 22
FEATURE [PartDesign::Chamfer] Chamfer
  Base = -> Pocket002 [Edge3]
  BaseFeature = -> Pocket002
  Size = 1.6
FEATURE [PartDesign::Body] Body  label="Knob001"
  Group = -> [Sketch,Sketch001,Pad,Sketch002,Pocket,Pocket001,Sketch003,Pocket002,Chamfer]
  Origin = -> Origin028
  Placement = pos=(0,0,1.4) rot=(0,0,1;0rad)
  Tip = -> Chamfer
FEATURE [App::Part] Part  label="Knob"
  Group = -> [Body]
  Origin = -> Origin025
  Placement = pos=(0,0,9.4) rot=(0,0,1;0rad)
FEATURE [Sketcher::SketchObject] Sketch005
  MapMode = 5
  Placement = pos=(0,0,4) rot=(0,0,1;0rad)
  Support = -> [Pad001]
  sketch-geometry (18):
    g0: ArcOfCircle CenterX=-23 CenterY=19 CenterZ=0 NormalX=0 NormalY=0 NormalZ=1 AngleXU=0 Radius=3 StartAngle=4.01636 EndAngle=7.16912
    g1: ArcOfCircle CenterX=-23 CenterY=-19 CenterZ=0 NormalX=0 NormalY=0 NormalZ=1 AngleXU=0 Radius=3 StartAngle=5.39725 EndAngle=8.55001
    g2: ArcOfCircle CenterX=23 CenterY=-19 CenterZ=0 NormalX=0 NormalY=0 NormalZ=1 AngleXU=0 Radius=3 StartAngle=0.874763 EndAngle=4.02753
    g3: ArcOfCircle CenterX=23 CenterY=19 CenterZ=0 NormalX=0 NormalY=0 NormalZ=1 AngleXU=0 Radius=3 StartAngle=2.25566 EndAngle=5.40842
    g4: ArcOfCircle CenterX=0 CenterY=0 CenterZ=0 NormalX=0 NormalY=0 NormalZ=1 AngleXU=0 Radius=33 StartAngle=3.32443 EndAngle=4.2062
    g5: ArcOfCircle CenterX=0 CenterY=0 CenterZ=0 NormalX=0 NormalY=0 NormalZ=1 AngleXU=0 Radius=30 StartAngle=2.55131 EndAngle=2.94023
    g6: ArcOfCircle CenterX=0 CenterY=0 CenterZ=0 NormalX=0 NormalY=0 NormalZ=1 AngleXU=0 Radius=30 StartAngle=3.9322 EndAngle=4.14985
    g7: ArcOfCircle CenterX=0 CenterY=0 CenterZ=0 NormalX=0 NormalY=0 NormalZ=1 AngleXU=0 Radius=30 StartAngle=5.6929 EndAngle=6.87347
    g8: ArcOfCircle CenterX=0 CenterY=0 CenterZ=0 NormalX=0 NormalY=0 NormalZ=1 AngleXU=0 Radius=30 StartAngle=0.790612 EndAngle=2.35098
    g9: LineSegment StartX=-32.45 StartY=6 StartZ=0 EndX=-29.3939 EndY=6 EndZ=0
    g10: LineSegment StartX=-32.45 StartY=-6 StartZ=0 EndX=-29.3939 EndY=-6 EndZ=0
    g11: LineSegment StartX=-16 StartY=-25.3772 StartZ=0 EndX=-16 EndY=-28.8617 EndZ=0
    g12: LineSegment StartX=16 StartY=-28.8617 StartZ=0 EndX=16 EndY=-25.3772 EndZ=0
    g13: ArcOfCircle CenterX=0 CenterY=0 CenterZ=0 NormalX=0 NormalY=0 NormalZ=1 AngleXU=0 Radius=30 StartAngle=5.27493 EndAngle=5.49257
    g14: ArcOfCircle CenterX=0 CenterY=0 CenterZ=0 NormalX=0 NormalY=0 NormalZ=1 AngleXU=0 Radius=30 StartAngle=3.34295 EndAngle=3.73187
    g15: LineSegment StartX=-13.7477 StartY=-30 StartZ=0 EndX=13.7477 EndY=-30 EndZ=0
    g16: ArcOfCircle CenterX=0 CenterY=0 CenterZ=0 NormalX=0 NormalY=0 NormalZ=1 AngleXU=0 Radius=33 StartAngle=4.28269 EndAngle=5.14209
    g17: ArcOfCircle CenterX=0 CenterY=0 CenterZ=0 NormalX=0 NormalY=0 NormalZ=1 AngleXU=0 Radius=33 StartAngle=5.21858 EndAngle=9.24194
  constraints (61):
    c: DistanceX(g0,g-1) = 23
    c: DistanceX(g-1,g3) = 23
    c: DistanceX(g1,g-1) = 23
    c: DistanceX(g-1,g2) = 23
    c: DistanceY(g-1,g0) = 19
    c: DistanceY(g1,g-1) = 19
    c: DistanceY(g-1,g3) = 19
    c: DistanceY(g2,g-1) = 19
    c: Radius(g3) = 3
    c: Radius(g2) = 3
    c: Radius(g1) = 3
    c: Radius(g0) = 3
    c: Coincident(g4,g-1)
    c: Radius(g4) = 33
    c: Radius(g5) = 30
    c: Coincident(g5,g-1)
    c: Coincident(g0,g5)
    c: Coincident(g0,g8)
    c: Equal(g5,g6)
    c: Coincident(g5,g6)
    c: Coincident(g1,g6)
    c: Coincident(g1,g14)
    c: Equal(g6,g7)
    c: Coincident(g6,g7)
    c: Coincident(g2,g7)
    c: Coincident(g2,g13)
    c: Equal(g7,g8)
    c: Coincident(g7,g8)
    c: Coincident(g3,g8)
    c: Coincident(g3,g7)
    c: Coincident(g9,g17)
    c: Horizontal(g9)
    c: Coincident(g10,g4)
    c: Horizontal(g10)
    c: Vertical(g11)
    c: Vertical(g12)
    c: PointOnObject(g12,g6)
    c: Equal(g6,g13)
    c: Coincident(g6,g11)
    c: Coincident(g6,g13)
    c: PointOnObject(g13,g12)
    c: Equal(g5,g14)
    c: Coincident(g5,g9)
    c: Coincident(g14,g10)
    c: Coincident(g5,g14)
    c: DistanceY(g-1,g17) = 6
    c: DistanceY(g4,g-1) = 6
    c: DistanceX(g-1,g12) = 16
    c: PointOnObject(g12,g4)
    c: Horizontal(g15)
    c: PointOnObject(g15,g4)
    c: Equal(g4,g16)
    c: Coincident(g4,g11)
    c: Coincident(g16,g15)
    c: Coincident(g4,g16)
    c: Equal(g16,g17)
    c: PointOnObject(g16,g15)
    c: PointOnObject(g17,g12)
    c: Coincident(g16,g17)
    c: DistanceX(g4,g4) = 16
    c: DistanceY(g15,g4) = 30
FEATURE [PartDesign::Pad] Pad009
  BaseFeature = -> Pad001
  Length = 2
  Length2 = 100
  Profile = -> Sketch005
  Type = 0
FEATURE [Sketcher::SketchObject] Sketch018  label="Sketch019"
  MapMode = 5
  Support = -> [XY_Plane053]
  sketch-geometry (2):
    g0: ArcOfCircle CenterX=0 CenterY=0 CenterZ=0 NormalX=0 NormalY=0 NormalZ=1 AngleXU=0 Radius=35 StartAngle=3.31387 EndAngle=9.2525
    g1: LineSegment StartX=-34.4819 StartY=6 StartZ=0 EndX=-34.4819 EndY=-6 EndZ=0
  constraints (7):
    c: Radius(g0) = 35
    c: Coincident(g-1,g0)
    c: Vertical(g1)
    c: Coincident(g0,g1)
    c: Coincident(g0,g1)
    c: Coincident(g0,g1)
    c: DistanceY(g1,g1) = 12
FEATURE [PartDesign::Pad] Pad010
  BaseFeature = -> Pad009
  Length = 2.4
  Length2 = 100
  Profile = -> Sketch018
  Type = 0
FEATURE [Sketcher::SketchObject] CopySketch013  label="Sketch020"
  sketch-geometry (20):
    g0: ArcOfCircle CenterX=0 CenterY=0 CenterZ=0 NormalX=0 NormalY=0 NormalZ=1 AngleXU=0 Radius=35 StartAngle=3.31387 EndAngle=9.2525
    g1: ArcOfCircle CenterX=0 CenterY=0 CenterZ=0 NormalX=0 NormalY=0 NormalZ=1 AngleXU=0 Radius=31.4 StartAngle=2.62899 EndAngle=2.88854
    g2: ArcOfCircle CenterX=-23 CenterY=-19 CenterZ=0 NormalX=0 NormalY=0 NormalZ=1 AngleXU=0 Radius=3.6 StartAngle=4.08385e-06 EndAngle=1.5708
    g3: ArcOfCircle CenterX=23 CenterY=-19 CenterZ=0 NormalX=0 NormalY=0 NormalZ=1 AngleXU=0 Radius=3.6 StartAngle=1.5708 EndAngle=3.14159
    g4: ArcOfCircle CenterX=-23 CenterY=19 CenterZ=0 NormalX=0 NormalY=0 NormalZ=1 AngleXU=0 Radius=3.6 StartAngle=4.71239 EndAngle=5.6975
    g5: ArcOfCircle CenterX=23 CenterY=19 CenterZ=0 NormalX=0 NormalY=0 NormalZ=1 AngleXU=0 Radius=3.6 StartAngle=3.14159 EndAngle=4.71239
    g6: LineSegment StartX=-20 StartY=24.2066 StartZ=0 EndX=-20 EndY=17.01 EndZ=0
    g7: LineSegment StartX=-23 StartY=15.4 StartZ=0 EndX=-27.3642 EndY=15.4 EndZ=0
    g8: LineSegment StartX=-27.3642 StartY=-15.4 StartZ=0 EndX=-23 EndY=-15.4 EndZ=0
    g9: LineSegment StartX=-19.4 StartY=-19 StartZ=0 EndX=-19.4 EndY=-24.6901 EndZ=0
    g10: LineSegment StartX=23 StartY=-15.4 StartZ=0 EndX=27.3642 EndY=-15.4 EndZ=0
    g11: LineSegment StartX=19.4 StartY=-19 StartZ=0 EndX=19.4 EndY=-24.6901 EndZ=0
    g12: LineSegment StartX=19.4 StartY=24.6901 StartZ=0 EndX=19.4 EndY=19 EndZ=0
    g13: LineSegment StartX=23 StartY=15.4 StartZ=0 EndX=27.3642 EndY=15.4 EndZ=0
    g14: ArcOfCircle CenterX=0 CenterY=0 CenterZ=0 NormalX=0 NormalY=0 NormalZ=1 AngleXU=0 Radius=31.4 StartAngle=4.0464 EndAngle=5.37837
    g15: ArcOfCircle CenterX=0 CenterY=0 CenterZ=0 NormalX=0 NormalY=0 NormalZ=1 AngleXU=0 Radius=31.4 StartAngle=5.77058 EndAngle=6.79579
    g16: ArcOfCircle CenterX=0 CenterY=0 CenterZ=0 NormalX=0 NormalY=0 NormalZ=1 AngleXU=0 Radius=31.4 StartAngle=0.904811 EndAngle=2.26132
    g17: LineSegment StartX=-34.4819 StartY=6 StartZ=0 EndX=-34.4819 EndY=-6 EndZ=0
    g18: LineSegment StartX=-30.4 StartY=7.8613 StartZ=0 EndX=-30.4 EndY=-7.8613 EndZ=0
    g19: ArcOfCircle CenterX=0 CenterY=0 CenterZ=0 NormalX=0 NormalY=0 NormalZ=1 AngleXU=0 Radius=31.4 StartAngle=3.39464 EndAngle=3.65419
  constraints (69):
    c: Radius(g0) = 35
    c: Coincident(g0,g-1)
    c: Radius(g1) = 31.4
    c: Coincident(g1,g0)
    c: Radius(g2) = 3.6
    c: DistanceY(g2,g0) = 19
    c: DistanceX(g2,g0) = 23
    c: Radius(g4) = 3.6
    c: Radius(g5) = 3.6
    c: Radius(g3) = 3.6
    c: DistanceY(g0,g4) = 19
    c: DistanceX(g4,g0) = 23
    c: DistanceX(g0,g5) = 23
    c: DistanceX(g0,g3) = 23
    c: DistanceY(g0,g5) = 19
    c: DistanceY(g3,g0) = 19
    c: Vertical(g6)
    c: Horizontal(g7)
    c: Vertical(g9)
    c: Horizontal(g8)
    c: PointOnObject(g10,g1)
    c: PointOnObject(g11,g1)
    c: Vertical(g11)
    c: Horizontal(g10)
    c: PointOnObject(g12,g1)
    c: PointOnObject(g13,g1)
    c: Horizontal(g13)
    c: Vertical(g12)
    c: Coincident(g2,g8)
    c: Coincident(g2,g9)
    c: Coincident(g3,g11)
    c: Coincident(g4,g7)
    c: Coincident(g4,g6)
    c: Coincident(g3,g10)
    c: DistanceY(g3,g3) = 3.6
    c: Coincident(g5,g12)
    c: DistanceX(g5,g5) = 3.6
    c: Coincident(g5,g13)
    c: DistanceY(g5,g5) = 3.6
    c: DistanceY(g2,g2) = 3.6
    c: DistanceX(g2,g2) = 3.6
    c: DistanceX(g4,g4) = 3
    c: DistanceY(g4,g4) = 3.6
    c: DistanceX(g3,g3) = 3.6
    c: Coincident(g1,g7)
    c: Coincident(g16,g6)
    c: Equal(g1,g14)
    c: Coincident(g19,g8)
    c: Coincident(g14,g9)
    c: Coincident(g1,g14)
    c: Equal(g14,g15)
    c: PointOnObject(g14,g11)
    c: PointOnObject(g15,g10)
    c: Coincident(g14,g15)
    c: Equal(g15,g16)
    c: PointOnObject(g15,g13)
    c: PointOnObject(g16,g12)
    c: Coincident(g15,g16)
    c: Vertical(g17)
    c: Coincident(g0,g17)
    c: DistanceY(g17,g17) = 12
    c: Coincident(g17,g0)
    c: Coincident(g17,g0)
    c: Vertical(g18)
    c: Equal(g1,g19)
    c: Coincident(g1,g18)
    c: Coincident(g19,g18)
    c: Coincident(g1,g19)
    c: DistanceX(g18,g0) = 30.4
FEATURE [PartDesign::Pad] Pad011
  Length = 10
  Length2 = 100
  Profile = -> CopySketch013
  Type = 0
FEATURE [Sketcher::SketchObject] Sketch019  label="Sketch021"
  MapMode = 5
  Support = -> [XY_Plane]
  sketch-geometry (4):
    g0: ArcOfCircle CenterX=0 CenterY=0 CenterZ=0 NormalX=0 NormalY=0 NormalZ=1 AngleXU=0 Radius=35 StartAngle=3.31387 EndAngle=9.2525
    g1: ArcOfCircle CenterX=0 CenterY=0 CenterZ=0 NormalX=0 NormalY=0 NormalZ=1 AngleXU=0 Radius=33.4 StartAngle=3.32221 EndAngle=9.24416
    g2: LineSegment StartX=-32.8567 StartY=6 StartZ=0 EndX=-32.8567 EndY=-6 EndZ=0
    g3: LineSegment StartX=-34.4819 StartY=6 StartZ=0 EndX=-34.4819 EndY=-6 EndZ=0
  constraints (14):
    c: Coincident(g0,g-1)
    c: Coincident(g1,g0)
    c: Radius(g0) = 35
    c: Radius(g1) = 33.4
    c: Vertical(g2)
    c: Vertical(g3)
    c: Coincident(g0,g3)
    c: Coincident(g0,g3)
    c: Coincident(g1,g2)
    c: Coincident(g1,g2)
    c: Coincident(g1,g2)
    c: Coincident(g0,g3)
    c: DistanceY(g3,g3) = 12
    c: DistanceY(g2,g2) = 12
FEATURE [PartDesign::Pad] Pad012
  BaseFeature = -> Pad011
  Length = 4.8
  Length2 = 100
  Profile = -> Sketch019
  Reversed = true
  Type = 0
FEATURE [Sketcher::SketchObject] Sketch021  label="Sketch023"
  MapMode = 5
  Placement = pos=(-34.4819,0,0) rot=(0.57735,-0.57735,-0.57735;2.0944rad)
  sketch-geometry (4):
    g0: ArcOfCircle CenterX=2.9 CenterY=1.68 CenterZ=0 NormalX=0 NormalY=0 NormalZ=1 AngleXU=0 Radius=2 StartAngle=4.71239 EndAngle=7.85398
    g1: ArcOfCircle CenterX=-2.9 CenterY=1.68 CenterZ=0 NormalX=0 NormalY=0 NormalZ=1 AngleXU=0 Radius=2 StartAngle=1.5708 EndAngle=4.71239
    g2: LineSegment StartX=2.9 StartY=3.68 StartZ=0 EndX=-2.9 EndY=3.68 EndZ=0
    g3: LineSegment StartX=2.9 StartY=-0.32 StartZ=0 EndX=-2.9 EndY=-0.32 EndZ=0
  constraints (10):
    c: Tangent(g0,g3) = 1.5708
    c: Tangent(g0,g2) = -1.5708
    c: Tangent(g2,g1) = -1.5708
    c: Tangent(g3,g1) = 1.5708
    c: Horizontal(g2)
    c: Equal(g0,g1)
    c: Radius(g1) = 2
    c: DistanceX(g1,g0) = 5.8
    c: DistanceX(g-1,g0) = 2.9
    c: DistanceY(g-1,g0) = 1.68
FEATURE [Sketcher::SketchObject] Sketch022  label="Sketch024"
  AttachmentOffset = pos=(0,0,35) rot=(0,0,1;0rad)
  MapMode = 5
  Placement = pos=(0,-35,-7.8e-15) rot=(1,0,0;1.5708rad)
  Support = -> [XZ_Plane]
  sketch-geometry (2):
    g0: Circle CenterX=-9.5 CenterY=4 CenterZ=0 NormalX=0 NormalY=0 NormalZ=1 AngleXU=0 Radius=3.4
    g1: Circle CenterX=9.5 CenterY=4 CenterZ=0 NormalX=0 NormalY=0 NormalZ=1 AngleXU=0 Radius=3.4
  constraints (6):
    c: Radius(g1) = 3.4
    c: Radius(g0) = 3.4
    c: DistanceY(g-1,g1) = 4
    c: DistanceY(g-1,g0) = 4
    c: DistanceX(g0,g1) = 19
    c: DistanceX(g0,g-1) = 9.5
FEATURE [Sketcher::SketchObject] Sketch023  label="Sketch025"
  AttachmentOffset = pos=(0,0,31) rot=(0,0,1;0rad)
  MapMode = 5
  Placement = pos=(0,-31,-6.9e-15) rot=(1,0,0;1.5708rad)
  Support = -> [XZ_Plane]
  sketch-geometry (4):
    g0: LineSegment StartX=-14 StartY=9 StartZ=0 EndX=14 EndY=9 EndZ=0
    g1: LineSegment StartX=14 StartY=9 StartZ=0 EndX=14 EndY=0 EndZ=0
    g2: LineSegment StartX=14 StartY=0 StartZ=0 EndX=-14 EndY=0 EndZ=0
    g3: LineSegment StartX=-14 StartY=0 StartZ=0 EndX=-14 EndY=9 EndZ=0
  constraints (12):
    c: Coincident(g0,g1)
    c: Coincident(g1,g2)
    c: Coincident(g2,g3)
    c: Coincident(g3,g0)
    c: Horizontal(g0)
    c: Horizontal(g2)
    c: Vertical(g1)
    c: Vertical(g3)
    c: DistanceX(g-1,g1) = 14
    c: DistanceX(g2,g1) = 28
    c: DistanceY(g-1,g0) = 9
    c: PointOnObject(g-1,g2)
FEATURE [Sketcher::SketchObject] Sketch024  label="Sketch026"
  MapMode = 5
  Placement = pos=(0,0,10) rot=(0,0,1;0rad)
  sketch-geometry (3):
    g0: ArcOfCircle CenterX=0 CenterY=0 CenterZ=0 NormalX=0 NormalY=0 NormalZ=1 AngleXU=0 Radius=35 StartAngle=3.31387 EndAngle=9.2525
    g1: Circle CenterX=0 CenterY=0 CenterZ=0 NormalX=0 NormalY=0 NormalZ=1 AngleXU=0 Radius=33.4
    g2: LineSegment StartX=-34.4819 StartY=6 StartZ=0 EndX=-34.4819 EndY=-6 EndZ=0
  constraints (9):
    c: Coincident(g0,g-1)
    c: Radius(g0) = 35
    c: Coincident(g1,g0)
    c: Radius(g1) = 33.4
    c: Vertical(g2)
    c: Coincident(g0,g2)
    c: Coincident(g0,g2)
    c: Coincident(g2,g0)
    c: DistanceY(g0,g0) = 12
FEATURE [PartDesign::Pad] Pad013
  BaseFeature = -> Pad012
  Length = 3.2
  Length2 = 100
  Profile = -> Sketch024
  Type = 0
FEATURE [Sketcher::SketchObject] Sketch020  label="Sketch022"
  MapMode = 5
  Placement = pos=(-30.4,0,0) rot=(0.57735,0.57735,0.57735;2.0944rad)
  Support = -> [Pad013]
  sketch-geometry (6):
    g0: ArcOfCircle CenterX=-4 CenterY=1.68 CenterZ=0 NormalX=0 NormalY=0 NormalZ=1 AngleXU=0 Radius=2 StartAngle=1.5708 EndAngle=3.14159
    g1: ArcOfCircle CenterX=4 CenterY=1.68 CenterZ=0 NormalX=0 NormalY=0 NormalZ=1 AngleXU=0 Radius=2 StartAngle=0 EndAngle=1.5708
    g2: LineSegment StartX=-4 StartY=3.68 StartZ=0 EndX=4 EndY=3.68 EndZ=0
    g3: LineSegment StartX=-6 StartY=1.68 StartZ=0 EndX=-6 EndY=-3.6 EndZ=0
    g4: LineSegment StartX=-6 StartY=-3.6 StartZ=0 EndX=6 EndY=-3.6 EndZ=0
    g5: LineSegment StartX=6 StartY=1.68 StartZ=0 EndX=6 EndY=-3.6 EndZ=0
  constraints (20):
    c: Radius(g1) = 2
    c: Radius(g0) = 2
    c: Coincident(g3,g4)
    c: Coincident(g5,g4)
    c: Horizontal(g2)
    c: Horizontal(g4)
    c: Vertical(g3)
    c: Vertical(g5)
    c: Coincident(g0,g2)
    c: Coincident(g0,g3)
    c: Coincident(g1,g5)
    c: Coincident(g1,g2)
    c: DistanceX(g-1,g4) = 6
    c: DistanceX(g3,g-1) = 6
    c: DistanceX(g0,g-1) = 4
    c: DistanceX(g-1,g1) = 4
    c: DistanceY(g-1,g1) = 1.68
    c: DistanceY(g-1,g0) = 1.68
    c: DistanceY(g-1,g1) = 3.68
    c: DistanceY(g4,g-1) = 3.6
FEATURE [PartDesign::Pocket] Pocket007
  BaseFeature = -> Pad013
  Length = 5
  Length2 = 100
  Profile = -> Sketch020
  Type = 2
FEATURE [PartDesign::Pocket] Pocket008
  BaseFeature = -> Pocket007
  Length = 5
  Length2 = 100
  Profile = -> Sketch021
  Type = 2
FEATURE [PartDesign::Pocket] Pocket009
  BaseFeature = -> Pocket008
  Length = 5
  Length2 = 100
  Profile = -> Sketch023
  Type = 0
FEATURE [PartDesign::Pocket] Pocket010
  BaseFeature = -> Pocket009
  Length = 5
  Length2 = 100
  Profile = -> Sketch022
  Type = 0
FEATURE [Sketcher::SketchObject] Sketch025  label="Sketch027"
  MapMode = 5
  Support = -> [XY_Plane]
  sketch-geometry (4):
    g0: Circle CenterX=-23 CenterY=19 CenterZ=0 NormalX=0 NormalY=0 NormalZ=1 AngleXU=0 Radius=0.8
    g1: Circle CenterX=23 CenterY=19 CenterZ=0 NormalX=0 NormalY=0 NormalZ=1 AngleXU=0 Radius=0.8
    g2: Circle CenterX=-23 CenterY=-19 CenterZ=0 NormalX=0 NormalY=0 NormalZ=1 AngleXU=0 Radius=0.8
    g3: Circle CenterX=23 CenterY=-19 CenterZ=0 NormalX=0 NormalY=0 NormalZ=1 AngleXU=0 Radius=0.8
  constraints (12):
    c: Diameter(g0) = 1.6
    c: DistanceX(g0,g-1) = 23
    c: DistanceY(g-1,g0) = 19
    c: Diameter(g1) = 1.6
    c: Diameter(g2) = 1.6
    c: Diameter(g3) = 1.6
    c: DistanceY(g2,g-1) = 19
    c: DistanceY(g3,g-1) = 19
    c: DistanceY(g-1,g1) = 19
    c: DistanceX(g-1,g1) = 23
    c: DistanceX(g-1,g3) = 23
    c: DistanceX(g2,g-1) = 23
FEATURE [PartDesign::Pocket] Pocket011
  BaseFeature = -> Pocket010
  Length = 0
  Length2 = 100
  Profile = -> Sketch025
  Reversed = true
  Type = 1
FEATURE [PartDesign::Body] Body007  label="MidFrame001"
  Group = -> [CopySketch013,Pad011,Sketch019,Pad012,Sketch020,Sketch021,Sketch022,Sketch023,Sketch024,Pad013,Pocket007,Pocket008,Pocket009,Pocket010,Sketch025,Pocket011]
  Origin = -> Origin
  Tip = -> Pocket011
FEATURE [App::Part] Part004  label="MidFrame"
  Group = -> [Body007]
  Origin = -> Origin084
FEATURE [Sketcher::SketchObject] Sketch026  label="Sketch028"
  MapMode = 5
  Support = -> [XY_Plane053]
  sketch-geometry (4):
    g0: Circle CenterX=-23 CenterY=19 CenterZ=0 NormalX=0 NormalY=0 NormalZ=1 AngleXU=0 Radius=0.8
    g1: Circle CenterX=23 CenterY=19 CenterZ=0 NormalX=0 NormalY=0 NormalZ=1 AngleXU=0 Radius=0.8
    g2: Circle CenterX=-23 CenterY=-19 CenterZ=0 NormalX=0 NormalY=0 NormalZ=1 AngleXU=0 Radius=0.8
    g3: Circle CenterX=23 CenterY=-19 CenterZ=0 NormalX=0 NormalY=0 NormalZ=1 AngleXU=0 Radius=0.8
  constraints (12):
    c: Diameter(g0) = 1.6
    c: DistanceY(g-1,g0) = 19
    c: DistanceX(g0,g-1) = 23
    c: Diameter(g1) = 1.6
    c: Diameter(g2) = 1.6
    c: Diameter(g3) = 1.6
    c: DistanceY(g-1,g1) = 19
    c: DistanceY(g2,g-1) = 19
    c: DistanceY(g3,g-1) = 19
    c: DistanceX(g-1,g3) = 23
    c: DistanceX(g2,g-1) = 23
    c: DistanceX(g-1,g1) = 23
FEATURE [PartDesign::Pocket] Pocket012
  BaseFeature = -> Pad010
  Length = 5
  Length2 = 100
  Profile = -> Sketch026
  Reversed = true
  Type = 1
FEATURE [Sketcher::SketchObject] Sketch027  label="Sketch029"
  MapMode = 5
  Support = -> [XY_Plane053]
  sketch-geometry (4):
    g0: Circle CenterX=-23 CenterY=19 CenterZ=0 NormalX=0 NormalY=0 NormalZ=1 AngleXU=0 Radius=2
    g1: Circle CenterX=23 CenterY=19 CenterZ=0 NormalX=0 NormalY=0 NormalZ=1 AngleXU=0 Radius=2
    g2: Circle CenterX=-23 CenterY=-19 CenterZ=0 NormalX=0 NormalY=0 NormalZ=1 AngleXU=0 Radius=2
    g3: Circle CenterX=23 CenterY=-19 CenterZ=0 NormalX=0 NormalY=0 NormalZ=1 AngleXU=0 Radius=2
  constraints (12):
    c: Diameter(g0) = 4
    c: DistanceY(g-1,g0) = 19
    c: DistanceX(g0,g-1) = 23
    c: Diameter(g1) = 4
    c: Diameter(g2) = 4
    c: Diameter(g3) = 4
    c: DistanceY(g-1,g1) = 19
    c: DistanceY(g2,g-1) = 19
    c: DistanceY(g3,g-1) = 19
    c: DistanceX(g-1,g3) = 23
    c: DistanceX(g2,g-1) = 23
    c: DistanceX(g-1,g1) = 23
FEATURE [PartDesign::Pocket] Pocket013
  BaseFeature = -> Pocket012
  Length = 2.4
  Length2 = 100
  Profile = -> Sketch027
  Reversed = true
  Type = 0
FEATURE [PartDesign::Body] Body001  label="Base001"
  Group = -> [Sketch004,Pad001,Sketch005,Pad009,Sketch018,Pad010,Sketch026,Pocket012,Sketch027,Pocket013]
  Origin = -> Origin053
  Tip = -> Pocket013
FEATURE [App::Part] Part002  label="Base"
  Group = -> [Body001]
  Origin = -> Origin027
  Placement = pos=(0,0,-7.6) rot=(0,0,1;0rad)
FEATURE [Mesh::Feature] Mesh003  label="Knob001 (Meshed)"
FEATURE [Mesh::Feature] Mesh  label="Base001 (Meshed)"
FEATURE [Mesh::Feature] Mesh004  label="MidFrame001 (Meshed)"
